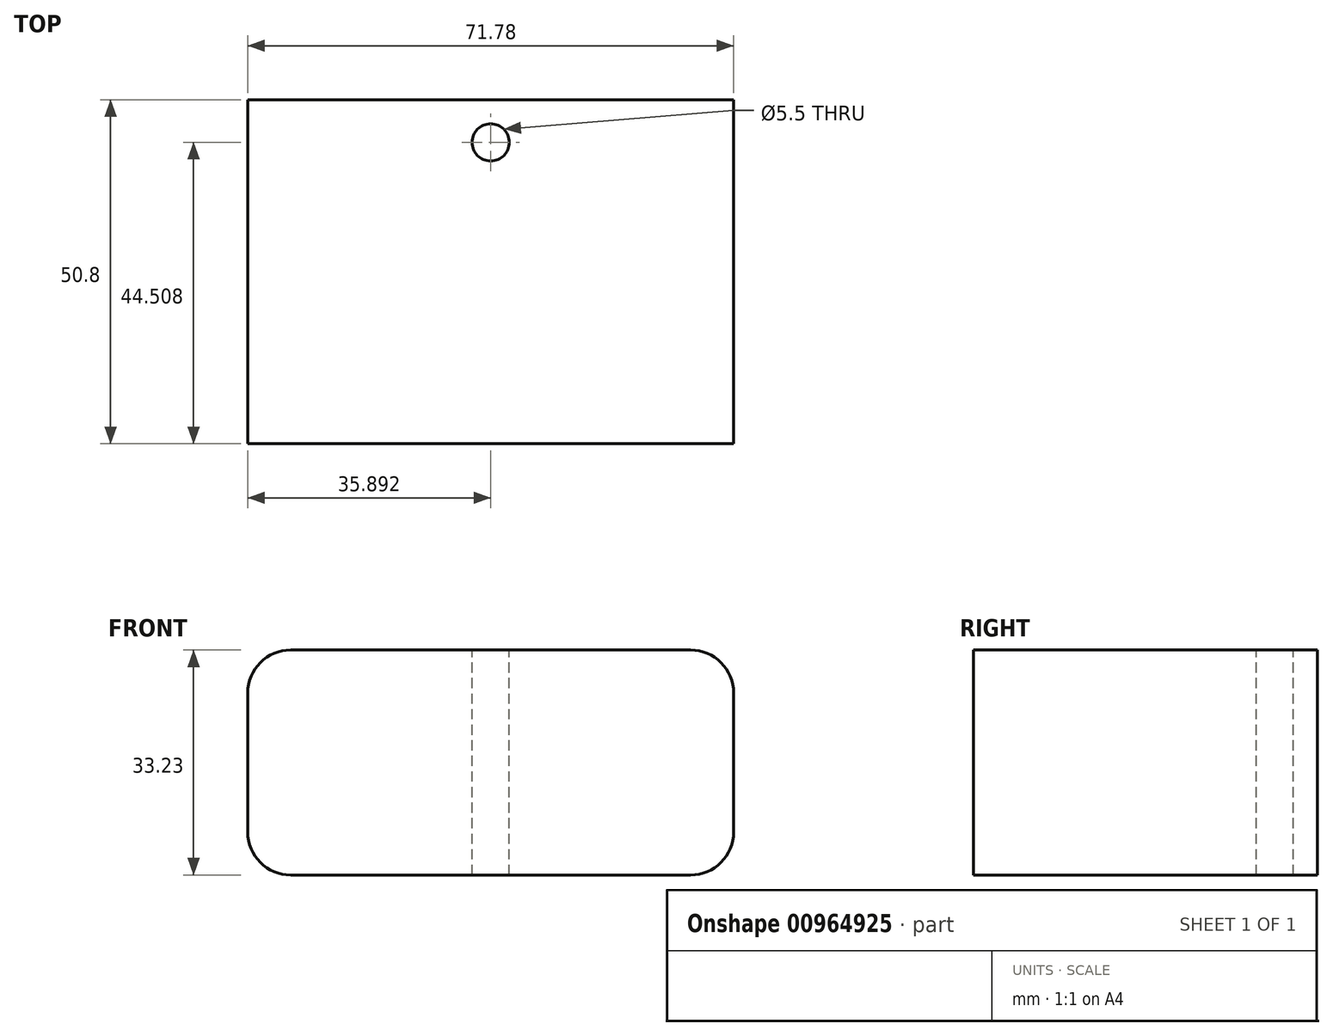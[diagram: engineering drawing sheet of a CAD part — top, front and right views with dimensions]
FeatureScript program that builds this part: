
annotation { "Feature Type Name" : "Feature", "Feature Type Description" : "" }
export const myFeature = defineFeature(function(context is Context, id is Id, definition is map)
    precondition{}
    {
        {
            var Q0;
            Q0=qCreatedBy(makeId("Front.planeOp"),FACE);
            var sketch = newSketch(context, id + "F0", { "sketchPlane" : qUnion([Q0])});
            skLineSegment(sketch, "E0.bottom", {"start": v(6.35, 0) * mm, "end": v(65.43, 0) * mm});
            skLineSegment(sketch, "E0.top", {"start": v(6.35, 33.23) * mm, "end": v(65.43, 33.23) * mm});
            skLineSegment(sketch, "E0.left", {"start": v(0, 6.35) * mm, "end": v(0, 26.88) * mm});
            skLineSegment(sketch, "E0.right", {"start": v(71.78, 6.35) * mm, "end": v(71.78, 26.88) * mm});
            skPoint(sketch, "E1.visualSharp", {"position": v(0, 33.23) * mm});
            skArc(sketch, "E1.filletArc", {"start": v(6.35, 33.23) * mm, "mid": v(1.86, 31.37) * mm, "end": v(0, 26.88) * mm});
            skPoint(sketch, "E2.visualSharp", {"position": v(71.78, 33.23) * mm});
            skArc(sketch, "E2.filletArc", {"start": v(71.78, 26.88) * mm, "mid": v(69.92, 31.37) * mm, "end": v(65.43, 33.23) * mm});
            skPoint(sketch, "E3.visualSharp", {"position": v(71.78, 0) * mm});
            skArc(sketch, "E3.filletArc", {"start": v(65.43, 0) * mm, "mid": v(69.92, 1.86) * mm, "end": v(71.78, 6.35) * mm});
            skPoint(sketch, "E4.visualSharp", {"position": v(0, 0) * mm});
            skArc(sketch, "E4.filletArc", {"start": v(0, 6.35) * mm, "mid": v(1.86, 1.86) * mm, "end": v(6.35, 0) * mm});
            skSolve(sketch);
        }
        {
            var Q0;
            Q0=makeQuery(id+"F0.imprint","IMPRINT",FACE,{"disambiguationData":[TD([[makeQuery(id+"F0.imprint","IMPRINT",EDGE,{"derivedFrom":sQuery(id+"F0.wireOp",EDGE,"E0.bottom")}),1.0]])]});
            extrude(context, id + "F1", {"entities" : qUnion([Q0]), "depth" : 50.8 * mm, "offsetDistance" : 25.4 * mm});
        }
        {
            var Q0;
            Q0=makeQuery(id+"F1.opExtrude","SWEPT_FACE",FACE,{"disambiguationData":[OSD([sQuery(id+"F0.wireOp",EDGE,"E0.top")])]});
            var sketch = newSketch(context, id + "F2", { "sketchPlane" : qUnion([Q0])});
            skCircle(sketch, "E5", {"center": v(35.9, -6.3) * mm, "radius": 2.3 * mm});
            skSolve(sketch);
        }
        {
            var Q0;
            Q0=sQuery(id+"F2.wireOp",VERTEX,"E5.center");
            var Q1;
            Q1=makeQuery(id+"F1.opExtrude","SWEPT_BODY",BODY,{"disambiguationData":[OSD([sQuery(id+"F0.wireOp",EDGE,"E0.bottom"),sQuery(id+"F0.wireOp",EDGE,"E0.top"),sQuery(id+"F0.wireOp",EDGE,"E0.left"),sQuery(id+"F0.wireOp",EDGE,"E0.right"),sQuery(id+"F0.wireOp",EDGE,"E1.filletArc"),sQuery(id+"F0.wireOp",EDGE,"E2.filletArc"),sQuery(id+"F0.wireOp",EDGE,"E3.filletArc"),sQuery(id+"F0.wireOp",EDGE,"E4.filletArc")])]});
            hole(context, id + "F3", {"style" : HoleStyle.SIMPLE, "endStyle" : HoleEndStyle.THROUGH, "standardTappedOrClearance" : lookupTablePath({ "fit" : "Normal", "standard" : "ISO", "size" : "M5", "type" : "Clearance" }), "standardBlindInLast" : lookupTablePath({ "fit" : "Normal", "standard" : "ISO", "engagement" : "75%", "pitch" : "0.8 mm", "size" : "M5", "type" : "Clearance & tapped" }), "holeDiameter" : 5.5 * mm, "majorDiameter" : 6.35 * mm, "isTappedThrough" : true, "tappedDepth" : 10 * mm, "tapClearance" : 3, "locations" : qUnion([Q0]), "scope" : qUnion([Q1])});
        }
    });
